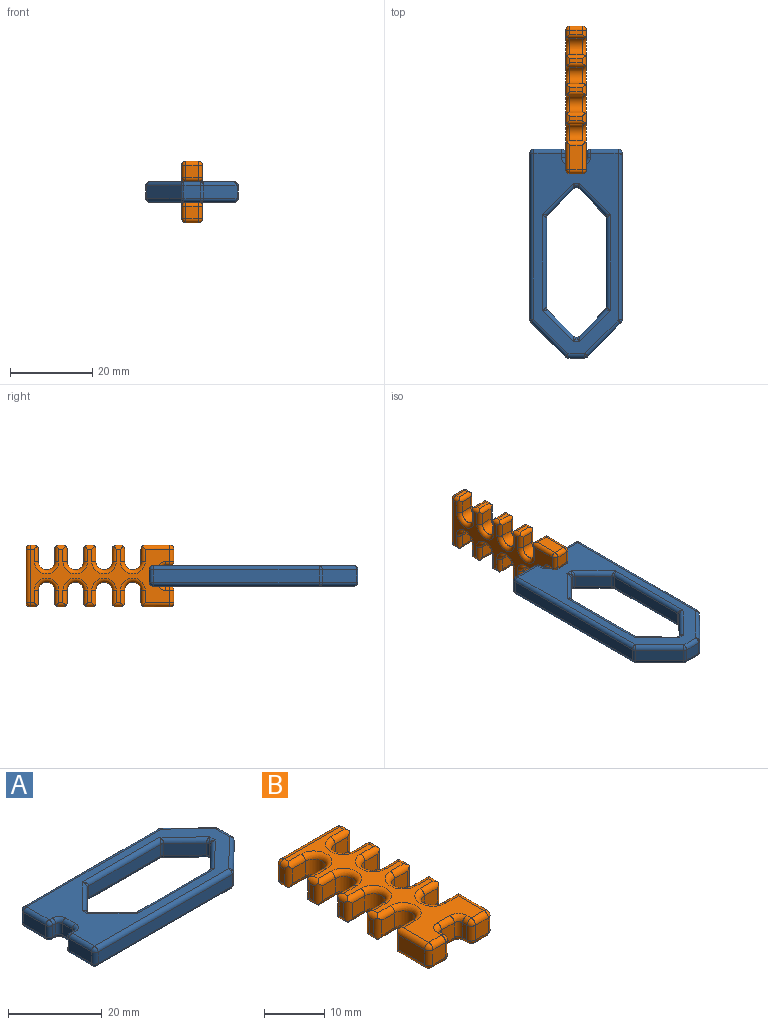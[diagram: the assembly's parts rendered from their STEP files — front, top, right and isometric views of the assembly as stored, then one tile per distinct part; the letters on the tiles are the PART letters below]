
ASSEMBLY  parts=2 mates=1
PART A: 108 faces, bbox 50.8x22.5x5 mm
  f0: plane 6.41x6.29mm, normal (-0.7,0.71,0), area 26.9mm2, adj f70,f78,f85,f97
  f1: plane 21.68x3mm, normal (0,1,0), area 65mm2, adj f68,f76,f85,f88
  f2: plane 6.41x6.29mm, normal (0.7,0.71,0), area 26.9mm2, adj f69,f77,f88,f106
  f3: plane 6.41x6.29mm, normal (0.7,-0.71,0), area 26.9mm2, adj f73,f81,f91,f103
  f4: plane 21.68x3mm, normal (0,-1,0), area 65mm2, adj f75,f83,f91,f94
  f5: plane 40.59x3mm, normal (0,1,0), area 121.8mm2, adj f56,f61,f64,f67
  f6: plane 6.75x3mm, normal (-1,0,0), area 20.3mm2, adj f53,f62,f63,f67
  f7: plane 3x1mm, normal (0,-1,0), area 3mm2, adj f43,f52,f53,f54
  f8: plane 3x3mm, normal (-1,0,0), area 9mm2, adj f33,f42,f43,f44
  f9: plane 3x1mm, normal (0,1,0), area 3mm2, adj f23,f32,f33,f34
  f10: plane 6.75x3mm, normal (-1,0,0), area 20.3mm2, adj f18,f22,f23,f24
  f11: plane 40.41x3mm, normal (0,-1,0), area 121.2mm2, adj f18,f21,f25,f26
  f12: plane 8.44x8.29mm, normal (0.7,-0.71,0), area 35.5mm2, adj f26,f31,f35,f36
  f13: plane 4.11x3mm, normal (1,0,0), area 12.3mm2, adj f36,f41,f45,f46
  f14: plane 8.26x8.11mm, normal (0.7,0.71,0), area 34.7mm2, adj f46,f51,f55,f56
  f15: plane 6.41x6.29mm, normal (-0.7,-0.71,0), area 26.9mm2, adj f74,f82,f94,f100
  f16: plane 48.85x20.5mm, normal (0,0,1), area 391.6mm2, adj f21,f22,f31,f32,f38,f41,f42,f48
  f17: plane 48.85x20.5mm, normal (0,0,-1), area 391.6mm2, adj f24,f25,f34,f35,f39,f44,f45,f49
  f18: cylinder r=1mm len=3mm, axis (0,0,-1), area 4.7mm2, adj f10,f11,f19,f20
  f19: sphere r=1mm, area 1.6mm2, adj f18,f21,f22
  f20: sphere r=1mm, area 1.6mm2, adj f18,f24,f25
  f21: cylinder r=1mm len=40.41mm, axis (-1,0,0), area 63.5mm2, adj f11,f16,f19,f27
  f22: cylinder r=1mm len=6.75mm, axis (0,1,0), area 10.6mm2, adj f10,f16,f19,f28
  f23: cylinder r=1mm len=3mm, axis (0,0,1), area 4.7mm2, adj f9,f10,f28,f29
  f24: cylinder r=1mm len=6.75mm, axis (0,-1,0), area 10.6mm2, adj f10,f17,f20,f29
  f25: cylinder r=1mm len=40.41mm, axis (1,0,0), area 63.5mm2, adj f11,f17,f20,f30
  f26: cylinder r=1mm len=3mm, axis (0,0,1), area 2.3mm2, adj f11,f12,f27,f30
  f27: sphere r=1mm, area 0.8mm2, adj f21,f26,f31
  f28: sphere r=1mm, area 1.6mm2, adj f22,f23,f32
  f29: sphere r=1mm, area 2.1mm2, adj f23,f24,f34
  f30: sphere r=1mm, area 0.8mm2, adj f25,f26,f35
  f31: cylinder r=1mm len=9.14mm, axis (-0.71,-0.7,0), area 18.6mm2, adj f12,f16,f27,f37
  f32: cylinder r=1mm len=1mm, axis (1,0,0), area 1.6mm2, adj f9,f16,f28,f38
  f33: cylinder r=1mm len=3mm, axis (0,0,1), area 4.7mm2, adj f8,f9,f38,f39
  f34: cylinder r=1mm len=1mm, axis (-1,0,0), area 1.6mm2, adj f9,f17,f29,f39
  f35: cylinder r=1mm len=9.14mm, axis (0.71,0.7,0), area 18.6mm2, adj f12,f17,f30,f40
  f36: cylinder r=1mm len=3mm, axis (0,0,-1), area 2.4mm2, adj f12,f13,f37,f40
  f37: sphere r=1mm, area 0.8mm2, adj f31,f36,f41
  f38: torus R=2mm, axis (0,0,1), area 3.4mm2, adj f16,f32,f33,f42
  f39: torus R=2mm, axis (0,0,1), area 3.4mm2, adj f17,f33,f34,f44
  f40: sphere r=1mm, area 0.8mm2, adj f35,f36,f45
  f41: cylinder r=1mm len=4.11mm, axis (0,-1,0), area 6.4mm2, adj f13,f16,f37,f47
  f42: cylinder r=1mm len=3mm, axis (0,1,0), area 4.7mm2, adj f8,f16,f38,f48
  f43: cylinder r=1mm len=3mm, axis (0,0,1), area 4.7mm2, adj f7,f8,f48,f49
  f44: cylinder r=1mm len=3mm, axis (0,-1,0), area 4.7mm2, adj f8,f17,f39,f49
  f45: cylinder r=1mm len=4.11mm, axis (0,1,0), area 6.4mm2, adj f13,f17,f40,f50
  f46: cylinder r=1mm len=3mm, axis (0,0,-1), area 2.4mm2, adj f13,f14,f47,f50
  f47: sphere r=1mm, area 1.1mm2, adj f41,f46,f51
  f48: torus R=2mm, axis (0,0,1), area 3.4mm2, adj f16,f42,f43,f52
  f49: torus R=2mm, axis (0,0,1), area 3.4mm2, adj f17,f43,f44,f54
  f50: sphere r=1mm, area 0.5mm2, adj f45,f46,f55
  f51: cylinder r=1mm len=8.96mm, axis (0.71,-0.7,0), area 18.2mm2, adj f14,f16,f47,f57
  f52: cylinder r=1mm len=1mm, axis (-1,0,0), area 1.6mm2, adj f7,f16,f48,f58
  f53: cylinder r=1mm len=3mm, axis (0,0,1), area 4.7mm2, adj f6,f7,f58,f59
  f54: cylinder r=1mm len=1mm, axis (1,0,0), area 1.6mm2, adj f7,f17,f49,f59
  f55: cylinder r=1mm len=8.96mm, axis (-0.71,0.7,0), area 18.2mm2, adj f14,f17,f50,f60
  f56: cylinder r=1mm len=3mm, axis (0,0,-1), area 2.3mm2, adj f5,f14,f57,f60
  f57: sphere r=1mm, area 1.1mm2, adj f51,f56,f61
  f58: sphere r=1mm, area 1.6mm2, adj f52,f53,f62
  f59: sphere r=1mm, area 1.6mm2, adj f53,f54,f63
  f60: sphere r=1mm, area 0.8mm2, adj f55,f56,f64
  f61: cylinder r=1mm len=40.59mm, axis (1,0,0), area 63.8mm2, adj f5,f16,f57,f65
  f62: cylinder r=1mm len=6.75mm, axis (0,1,0), area 10.6mm2, adj f6,f16,f58,f65
  f63: cylinder r=1mm len=6.75mm, axis (0,-1,0), area 10.6mm2, adj f6,f17,f59,f66
  f64: cylinder r=1mm len=40.59mm, axis (-1,0,0), area 63.8mm2, adj f5,f17,f60,f66
  f65: sphere r=1mm, area 2.1mm2, adj f61,f62,f67
  f66: sphere r=1mm, area 2.1mm2, adj f63,f64,f67
  f67: cylinder r=1mm len=3mm, axis (0,0,1), area 4.7mm2, adj f5,f6,f65,f66
  f68: cylinder r=1mm len=23.32mm, axis (-1,0,0), area 35.3mm2, adj f1,f17,f84,f87
  f69: cylinder r=1mm len=8.29mm, axis (-0.71,0.7,0), area 15.4mm2, adj f2,f17,f87,f104
  f70: cylinder r=1mm len=8.29mm, axis (-0.71,-0.7,0), area 15.4mm2, adj f0,f17,f84,f96
  f71: cylinder r=1mm len=1.59mm, axis (0,1,0), area 1mm2, adj f17,f102,f104
  f72: cylinder r=1mm len=1.59mm, axis (0,-1,0), area 1mm2, adj f17,f96,f98
  f73: cylinder r=1mm len=8.29mm, axis (0.71,0.7,0), area 15.4mm2, adj f3,f17,f90,f102
  f74: cylinder r=1mm len=8.29mm, axis (0.71,-0.7,0), area 15.4mm2, adj f15,f17,f93,f98
  f75: cylinder r=1mm len=23.32mm, axis (1,0,0), area 35.3mm2, adj f4,f17,f90,f93
  f76: cylinder r=1mm len=23.32mm, axis (1,0,0), area 35.3mm2, adj f1,f16,f86,f89
  f77: cylinder r=1mm len=8.29mm, axis (0.71,-0.7,0), area 15.4mm2, adj f2,f16,f89,f107
  f78: cylinder r=1mm len=8.29mm, axis (0.71,0.7,0), area 15.4mm2, adj f0,f16,f86,f99
  f79: cylinder r=1mm len=1.59mm, axis (0,-1,0), area 1mm2, adj f16,f105,f107
  f80: cylinder r=1mm len=1.59mm, axis (0,1,0), area 1mm2, adj f16,f99,f101
  f81: cylinder r=1mm len=8.29mm, axis (-0.71,-0.7,0), area 15.4mm2, adj f3,f16,f92,f105
  f82: cylinder r=1mm len=8.29mm, axis (-0.71,0.7,0), area 15.4mm2, adj f15,f16,f95,f101
  f83: cylinder r=1mm len=23.32mm, axis (-1,0,0), area 35.3mm2, adj f4,f16,f92,f95
  f84: bspline ~1.29x1.13mm, area 0.5mm2, adj f68,f70,f85
  f85: cylinder r=1mm len=3mm, axis (0,0,-1), area 2.3mm2, adj f0,f1,f84,f86
  f86: bspline ~1.29x1.13mm, area 0.5mm2, adj f76,f78,f85
  f87: bspline ~1.29x1.13mm, area 0.5mm2, adj f68,f69,f88
  f88: cylinder r=1mm len=3mm, axis (0,0,-1), area 2.3mm2, adj f1,f2,f87,f89
  f89: bspline ~1.29x1.13mm, area 0.5mm2, adj f76,f77,f88
  f90: bspline ~1.29x1.13mm, area 0.5mm2, adj f73,f75,f91
  f91: cylinder r=1mm len=3mm, axis (0,0,1), area 2.3mm2, adj f3,f4,f90,f92
  f92: bspline ~1.29x1.13mm, area 0.5mm2, adj f81,f83,f91
  f93: bspline ~1.29x1.13mm, area 0.5mm2, adj f74,f75,f94
  f94: cylinder r=1mm len=3mm, axis (0,0,1), area 2.3mm2, adj f4,f15,f93,f95
  f95: bspline ~1.29x1.13mm, area 0.5mm2, adj f82,f83,f94
  f96: bspline ~1.3x1.13mm, area 0.8mm2, adj f70,f72,f97,f98
  f97: cylinder r=1mm len=3mm, axis (0,0,1), area 2.2mm2, adj f0,f96,f99,f100
  f98: bspline ~1.3x1.13mm, area 0.8mm2, adj f72,f74,f96,f100
  f99: bspline ~1.3x1.13mm, area 0.8mm2, adj f78,f80,f97,f101
  f100: cylinder r=1mm len=3mm, axis (0,0,1), area 2.2mm2, adj f15,f97,f98,f101
  f101: bspline ~1.3x1.13mm, area 0.8mm2, adj f80,f82,f99,f100
  f102: bspline ~1.3x1.13mm, area 0.8mm2, adj f71,f73,f103,f104
  f103: cylinder r=1mm len=3mm, axis (0,0,-1), area 2.2mm2, adj f3,f102,f105,f106
  f104: bspline ~1.3x1.13mm, area 0.8mm2, adj f69,f71,f102,f106
  f105: bspline ~1.3x1.13mm, area 0.8mm2, adj f79,f81,f103,f107
  f106: cylinder r=1mm len=3mm, axis (0,0,-1), area 2.2mm2, adj f2,f103,f104,f107
  f107: bspline ~1.3x1.13mm, area 0.8mm2, adj f77,f79,f105,f106
PART B: 162 faces, bbox 15x36x5 mm
  f0: plane 3x3mm, normal (0,1,0), area 9mm2, adj f1,f110,f113,f146
  f1: cylinder r=2mm len=4mm, axis (0,0,-1), area 18.8mm2, adj f0,f2,f114,f117
  f2: plane 3x3mm, normal (0,-1,0), area 9mm2, adj f1,f118,f121,f147
  f3: plane 3x1mm, normal (1,0,0), area 3mm2, adj f122,f125,f147,f148
  f4: plane 3x3mm, normal (0,1,0), area 9mm2, adj f5,f126,f129,f148
  f5: cylinder r=2mm len=4mm, axis (0,0,-1), area 18.8mm2, adj f4,f6,f130,f134
  f6: plane 3x3mm, normal (0,-1,0), area 9mm2, adj f5,f135,f138,f161
  f7: plane 3x1mm, normal (1,0,0), area 3mm2, adj f139,f142,f145,f161
  f8: plane 13x3mm, normal (0,1,0), area 39mm2, adj f132,f140,f141,f145
  f9: plane 3x1mm, normal (-1,0,0), area 3mm2, adj f131,f132,f133,f160
  f10: plane 3x3mm, normal (0,-1,0), area 9mm2, adj f11,f127,f128,f160
  f11: cylinder r=2mm len=4mm, axis (0,0,-1), area 18.8mm2, adj f10,f12,f123,f124
  f12: plane 3x3mm, normal (0,1,0), area 9mm2, adj f11,f119,f120,f149
  f13: plane 3x1mm, normal (-1,0,0), area 3mm2, adj f115,f116,f149,f150
  f14: plane 3x3mm, normal (0,-1,0), area 9mm2, adj f15,f111,f112,f150
  f15: cylinder r=2mm len=4mm, axis (0,0,-1), area 18.8mm2, adj f14,f16,f107,f108
  f16: plane 3x3mm, normal (0,1,0), area 9mm2, adj f15,f103,f104,f151
  f17: plane 3x1mm, normal (-1,0,0), area 3mm2, adj f99,f100,f151,f152
  f18: plane 3x3mm, normal (0,-1,0), area 9mm2, adj f19,f95,f96,f152
  f19: cylinder r=2mm len=4mm, axis (0,0,-1), area 18.8mm2, adj f18,f20,f91,f92
  f20: plane 3x3mm, normal (0,1,0), area 9mm2, adj f19,f87,f88,f153
  f21: plane 3x1mm, normal (-1,0,0), area 3mm2, adj f83,f84,f153,f154
  f22: plane 3x3mm, normal (0,-1,0), area 9mm2, adj f23,f79,f80,f154
  f23: cylinder r=2mm len=4mm, axis (0,0,-1), area 18.8mm2, adj f22,f24,f75,f76
  f24: plane 3x3mm, normal (0,1,0), area 9mm2, adj f23,f71,f72,f159
  f25: plane 6x3mm, normal (-1,0,0), area 18mm2, adj f57,f66,f67,f159
  f26: plane 3x3mm, normal (0,-1,0), area 9mm2, adj f47,f56,f57,f58
  f27: plane 3x1mm, normal (1,0,0), area 3mm2, adj f42,f46,f47,f48
  f28: plane 3x3mm, normal (0,-1,0), area 9mm2, adj f42,f45,f49,f50
  f29: plane 3x1mm, normal (-1,0,0), area 3mm2, adj f50,f55,f59,f60
  f30: plane 3x3mm, normal (0,-1,0), area 9mm2, adj f60,f65,f68,f69
  f31: plane 6x3mm, normal (1,0,0), area 18mm2, adj f69,f74,f77,f158
  f32: plane 3x3mm, normal (0,1,0), area 9mm2, adj f33,f78,f81,f158
  f33: cylinder r=2mm len=4mm, axis (0,0,-1), area 18.8mm2, adj f32,f34,f82,f85
  f34: plane 3x3mm, normal (0,-1,0), area 9mm2, adj f33,f86,f89,f155
  f35: plane 3x1mm, normal (1,0,0), area 3mm2, adj f90,f93,f155,f156
  f36: plane 3x3mm, normal (0,1,0), area 9mm2, adj f37,f94,f97,f156
  f37: cylinder r=2mm len=4mm, axis (0,0,-1), area 18.8mm2, adj f36,f38,f98,f101
  f38: plane 3x3mm, normal (0,-1,0), area 9mm2, adj f37,f102,f105,f157
  f39: plane 3x1mm, normal (1,0,0), area 3mm2, adj f106,f109,f146,f157
  f40: plane 34x13mm, normal (0,0,1), area 165.6mm2, adj f43,f45,f46,f51,f55,f56,f65,f66
  f41: plane 34x13mm, normal (0,0,-1), area 165.6mm2, adj f44,f48,f49,f54,f58,f59,f67,f68
  f42: cylinder r=1mm len=3mm, axis (0,0,1), area 4.7mm2, adj f27,f28,f43,f44
  f43: torus R=2mm, axis (0,0,1), area 3.4mm2, adj f40,f42,f45,f46
  f44: torus R=2mm, axis (0,0,1), area 3.4mm2, adj f41,f42,f48,f49
  f45: cylinder r=1mm len=3mm, axis (-1,0,0), area 4.7mm2, adj f28,f40,f43,f51
  f46: cylinder r=1mm len=1mm, axis (0,-1,0), area 1.6mm2, adj f27,f40,f43,f52
  f47: cylinder r=1mm len=3mm, axis (0,0,-1), area 4.7mm2, adj f26,f27,f52,f53
  f48: cylinder r=1mm len=1mm, axis (0,1,0), area 1.6mm2, adj f27,f41,f44,f53
  f49: cylinder r=1mm len=3mm, axis (1,0,0), area 4.7mm2, adj f28,f41,f44,f54
  f50: cylinder r=1mm len=3mm, axis (0,0,1), area 4.7mm2, adj f28,f29,f51,f54
  f51: torus R=2mm, axis (0,0,1), area 3.4mm2, adj f40,f45,f50,f55
  f52: sphere r=1mm, area 1.6mm2, adj f46,f47,f56
  f53: sphere r=1mm, area 1.6mm2, adj f47,f48,f58
  f54: torus R=2mm, axis (0,0,1), area 3.4mm2, adj f41,f49,f50,f59
  f55: cylinder r=1mm len=1mm, axis (0,1,0), area 1.6mm2, adj f29,f40,f51,f61
  f56: cylinder r=1mm len=3mm, axis (-1,0,0), area 4.7mm2, adj f26,f40,f52,f62
  f57: cylinder r=1mm len=3mm, axis (0,0,1), area 4.7mm2, adj f25,f26,f62,f63
  f58: cylinder r=1mm len=3mm, axis (1,0,0), area 4.7mm2, adj f26,f41,f53,f63
  f59: cylinder r=1mm len=1mm, axis (0,-1,0), area 1.6mm2, adj f29,f41,f54,f64
  f60: cylinder r=1mm len=3mm, axis (0,0,-1), area 4.7mm2, adj f29,f30,f61,f64
  f61: sphere r=1mm, area 1.6mm2, adj f55,f60,f65
  f62: sphere r=1mm, area 1.6mm2, adj f56,f57,f66
  f63: sphere r=1mm, area 1.6mm2, adj f57,f58,f67
  f64: sphere r=1mm, area 1.6mm2, adj f59,f60,f68
  f65: cylinder r=1mm len=3mm, axis (-1,0,0), area 4.7mm2, adj f30,f40,f61,f70
  f66: cylinder r=1mm len=6.71mm, axis (0,1,0), area 10mm2, adj f25,f40,f62,f71,f159
  f67: cylinder r=1mm len=6.71mm, axis (0,-1,0), area 10mm2, adj f25,f41,f63,f72,f159
  f68: cylinder r=1mm len=3mm, axis (1,0,0), area 4.7mm2, adj f30,f41,f64,f73
  f69: cylinder r=1mm len=3mm, axis (0,0,-1), area 4.7mm2, adj f30,f31,f70,f73
  f70: sphere r=1mm, area 1.6mm2, adj f65,f69,f74
  f71: cylinder r=1mm len=3.71mm, axis (1,0,0), area 5.3mm2, adj f24,f40,f66,f75,f159
  f72: cylinder r=1mm len=3.71mm, axis (-1,0,0), area 5.3mm2, adj f24,f41,f67,f76,f159
  f73: sphere r=1mm, area 1.6mm2, adj f68,f69,f77
  f74: cylinder r=1mm len=6.71mm, axis (0,-1,0), area 10mm2, adj f31,f40,f70,f78,f158
  f75: torus R=3mm, axis (0,0,1), area 11.7mm2, adj f23,f40,f71,f79
  f76: torus R=3mm, axis (0,0,1), area 11.7mm2, adj f23,f41,f72,f80
  f77: cylinder r=1mm len=6.71mm, axis (0,1,0), area 10mm2, adj f31,f41,f73,f81,f158
  f78: cylinder r=1mm len=3.71mm, axis (1,0,0), area 5.3mm2, adj f32,f40,f74,f82,f158
  f79: cylinder r=1mm len=3.71mm, axis (-1,0,0), area 5.3mm2, adj f22,f40,f75,f83,f154
  f80: cylinder r=1mm len=3.71mm, axis (1,0,0), area 5.3mm2, adj f22,f41,f76,f84,f154
  f81: cylinder r=1mm len=3.71mm, axis (-1,0,0), area 5.3mm2, adj f32,f41,f77,f85,f158
  f82: torus R=3mm, axis (0,0,1), area 11.7mm2, adj f33,f40,f78,f86
  f83: cylinder r=1mm len=2.41mm, axis (0,1,0), area 2.7mm2, adj f21,f40,f79,f87,f153,f154
  f84: cylinder r=1mm len=2.41mm, axis (0,-1,0), area 2.7mm2, adj f21,f41,f80,f88,f153,f154
  f85: torus R=3mm, axis (0,0,1), area 11.7mm2, adj f33,f41,f81,f89
  f86: cylinder r=1mm len=3.71mm, axis (-1,0,0), area 5.3mm2, adj f34,f40,f82,f90,f155
  f87: cylinder r=1mm len=3.71mm, axis (1,0,0), area 5.3mm2, adj f20,f40,f83,f91,f153
  f88: cylinder r=1mm len=3.71mm, axis (-1,0,0), area 5.3mm2, adj f20,f41,f84,f92,f153
  f89: cylinder r=1mm len=3.71mm, axis (1,0,0), area 5.3mm2, adj f34,f41,f85,f93,f155
  f90: cylinder r=1mm len=2.41mm, axis (0,-1,0), area 2.7mm2, adj f35,f40,f86,f94,f155,f156
  f91: torus R=3mm, axis (0,0,1), area 11.7mm2, adj f19,f40,f87,f95
  f92: torus R=3mm, axis (0,0,1), area 11.7mm2, adj f19,f41,f88,f96
  f93: cylinder r=1mm len=2.41mm, axis (0,1,0), area 2.7mm2, adj f35,f41,f89,f97,f155,f156
  f94: cylinder r=1mm len=3.71mm, axis (1,0,0), area 5.3mm2, adj f36,f40,f90,f98,f156
  f95: cylinder r=1mm len=3.71mm, axis (-1,0,0), area 5.3mm2, adj f18,f40,f91,f99,f152
  f96: cylinder r=1mm len=3.71mm, axis (1,0,0), area 5.3mm2, adj f18,f41,f92,f100,f152
  f97: cylinder r=1mm len=3.71mm, axis (-1,0,0), area 5.3mm2, adj f36,f41,f93,f101,f156
  f98: torus R=3mm, axis (0,0,1), area 11.7mm2, adj f37,f40,f94,f102
  f99: cylinder r=1mm len=2.41mm, axis (0,1,0), area 2.7mm2, adj f17,f40,f95,f103,f151,f152
  f100: cylinder r=1mm len=2.41mm, axis (0,-1,0), area 2.7mm2, adj f17,f41,f96,f104,f151,f152
  f101: torus R=3mm, axis (0,0,1), area 11.7mm2, adj f37,f41,f97,f105
  f102: cylinder r=1mm len=3.71mm, axis (-1,0,0), area 5.3mm2, adj f38,f40,f98,f106,f157
  f103: cylinder r=1mm len=3.71mm, axis (1,0,0), area 5.3mm2, adj f16,f40,f99,f107,f151
  f104: cylinder r=1mm len=3.71mm, axis (-1,0,0), area 5.3mm2, adj f16,f41,f100,f108,f151
  f105: cylinder r=1mm len=3.71mm, axis (1,0,0), area 5.3mm2, adj f38,f41,f101,f109,f157
  f106: cylinder r=1mm len=2.41mm, axis (0,-1,0), area 2.7mm2, adj f39,f40,f102,f110,f146,f157
  f107: torus R=3mm, axis (0,0,1), area 11.7mm2, adj f15,f40,f103,f111
  f108: torus R=3mm, axis (0,0,1), area 11.7mm2, adj f15,f41,f104,f112
  f109: cylinder r=1mm len=2.41mm, axis (0,1,0), area 2.7mm2, adj f39,f41,f105,f113,f146,f157
  f110: cylinder r=1mm len=3.71mm, axis (1,0,0), area 5.3mm2, adj f0,f40,f106,f114,f146
  f111: cylinder r=1mm len=3.71mm, axis (-1,0,0), area 5.3mm2, adj f14,f40,f107,f115,f150
  f112: cylinder r=1mm len=3.71mm, axis (1,0,0), area 5.3mm2, adj f14,f41,f108,f116,f150
  f113: cylinder r=1mm len=3.71mm, axis (-1,0,0), area 5.3mm2, adj f0,f41,f109,f117,f146
  f114: torus R=3mm, axis (0,0,1), area 11.7mm2, adj f1,f40,f110,f118
  f115: cylinder r=1mm len=2.41mm, axis (0,1,0), area 2.7mm2, adj f13,f40,f111,f119,f149,f150
  f116: cylinder r=1mm len=2.41mm, axis (0,-1,0), area 2.7mm2, adj f13,f41,f112,f120,f149,f150
  f117: torus R=3mm, axis (0,0,1), area 11.7mm2, adj f1,f41,f113,f121
  f118: cylinder r=1mm len=3.71mm, axis (-1,0,0), area 5.3mm2, adj f2,f40,f114,f122,f147
  f119: cylinder r=1mm len=3.71mm, axis (1,0,0), area 5.3mm2, adj f12,f40,f115,f123,f149
  f120: cylinder r=1mm len=3.71mm, axis (-1,0,0), area 5.3mm2, adj f12,f41,f116,f124,f149
  f121: cylinder r=1mm len=3.71mm, axis (1,0,0), area 5.3mm2, adj f2,f41,f117,f125,f147
  f122: cylinder r=1mm len=2.41mm, axis (0,-1,0), area 2.7mm2, adj f3,f40,f118,f126,f147,f148
  f123: torus R=3mm, axis (0,0,1), area 11.7mm2, adj f11,f40,f119,f127
  f124: torus R=3mm, axis (0,0,1), area 11.7mm2, adj f11,f41,f120,f128
  f125: cylinder r=1mm len=2.41mm, axis (0,1,0), area 2.7mm2, adj f3,f41,f121,f129,f147,f148
  f126: cylinder r=1mm len=3.71mm, axis (1,0,0), area 5.3mm2, adj f4,f40,f122,f130,f148
  f127: cylinder r=1mm len=3.71mm, axis (-1,0,0), area 5.3mm2, adj f10,f40,f123,f131,f160
  f128: cylinder r=1mm len=3.71mm, axis (1,0,0), area 5.3mm2, adj f10,f41,f124,f133,f160
  f129: cylinder r=1mm len=3.71mm, axis (-1,0,0), area 5.3mm2, adj f4,f41,f125,f134,f148
  f130: torus R=3mm, axis (0,0,1), area 11.7mm2, adj f5,f40,f126,f135
  f131: cylinder r=1mm len=1.71mm, axis (0,1,0), area 2.2mm2, adj f9,f40,f127,f136,f160
  f132: cylinder r=1mm len=3mm, axis (0,0,-1), area 4.7mm2, adj f8,f9,f136,f137
  f133: cylinder r=1mm len=1.71mm, axis (0,-1,0), area 2.2mm2, adj f9,f41,f128,f137,f160
  f134: torus R=3mm, axis (0,0,1), area 11.7mm2, adj f5,f41,f129,f138
  f135: cylinder r=1mm len=3.71mm, axis (-1,0,0), area 5.3mm2, adj f6,f40,f130,f139,f161
  f136: sphere r=1mm, area 1.6mm2, adj f131,f132,f140
  f137: sphere r=1mm, area 1.6mm2, adj f132,f133,f141
  f138: cylinder r=1mm len=3.71mm, axis (1,0,0), area 5.3mm2, adj f6,f41,f134,f142,f161
  f139: cylinder r=1mm len=1.71mm, axis (0,-1,0), area 2.2mm2, adj f7,f40,f135,f143,f161
  f140: cylinder r=1mm len=13mm, axis (1,0,0), area 20.4mm2, adj f8,f40,f136,f143
  f141: cylinder r=1mm len=13mm, axis (-1,0,0), area 20.4mm2, adj f8,f41,f137,f144
  f142: cylinder r=1mm len=1.71mm, axis (0,1,0), area 2.2mm2, adj f7,f41,f138,f144,f161
  f143: sphere r=1mm, area 1.6mm2, adj f139,f140,f145
  f144: sphere r=1mm, area 1.6mm2, adj f141,f142,f145
  f145: cylinder r=1mm len=3mm, axis (0,0,1), area 4.7mm2, adj f7,f8,f143,f144
  f146: cylinder r=1mm len=4.41mm, axis (0,0,1), area 5.9mm2, adj f0,f39,f106,f109,f110,f113
  f147: cylinder r=1mm len=4.41mm, axis (0,0,-1), area 5.9mm2, adj f2,f3,f118,f121,f122,f125
  f148: cylinder r=1mm len=4.41mm, axis (0,0,1), area 5.9mm2, adj f3,f4,f122,f125,f126,f129
  f149: cylinder r=1mm len=4.41mm, axis (0,0,-1), area 5.9mm2, adj f12,f13,f115,f116,f119,f120
  f150: cylinder r=1mm len=4.41mm, axis (0,0,1), area 5.9mm2, adj f13,f14,f111,f112,f115,f116
  f151: cylinder r=1mm len=4.41mm, axis (0,0,-1), area 5.9mm2, adj f16,f17,f99,f100,f103,f104
  f152: cylinder r=1mm len=4.41mm, axis (0,0,1), area 5.9mm2, adj f17,f18,f95,f96,f99,f100
  f153: cylinder r=1mm len=4.41mm, axis (0,0,-1), area 5.9mm2, adj f20,f21,f83,f84,f87,f88
  f154: cylinder r=1mm len=4.41mm, axis (0,0,1), area 5.9mm2, adj f21,f22,f79,f80,f83,f84
  f155: cylinder r=1mm len=4.41mm, axis (0,0,-1), area 5.9mm2, adj f34,f35,f86,f89,f90,f93
  f156: cylinder r=1mm len=4.41mm, axis (0,0,1), area 5.9mm2, adj f35,f36,f90,f93,f94,f97
  f157: cylinder r=1mm len=4.41mm, axis (0,0,-1), area 5.9mm2, adj f38,f39,f102,f105,f106,f109
  f158: cylinder r=1mm len=4.41mm, axis (0,0,1), area 5.9mm2, adj f31,f32,f74,f77,f78,f81
  f159: cylinder r=1mm len=4.41mm, axis (0,0,-1), area 5.9mm2, adj f24,f25,f66,f67,f71,f72
  f160: cylinder r=1mm len=4.41mm, axis (0,0,1), area 5.9mm2, adj f9,f10,f127,f128,f131,f133
  f161: cylinder r=1mm len=4.41mm, axis (0,0,-1), area 5.9mm2, adj f6,f7,f135,f138,f139,f142
PLACE A rot(axis=(0,0,-1),90deg) t=(-36.29,-20.46,2.53)mm
PLACE B rot(axis=(0,1,0),90deg) t=(-38.88,13.63,5.03)mm
MATE fastened B.f28 <-> A.f8  axis (0,-1,0) through (-36.38,4.13,5.03)mm
